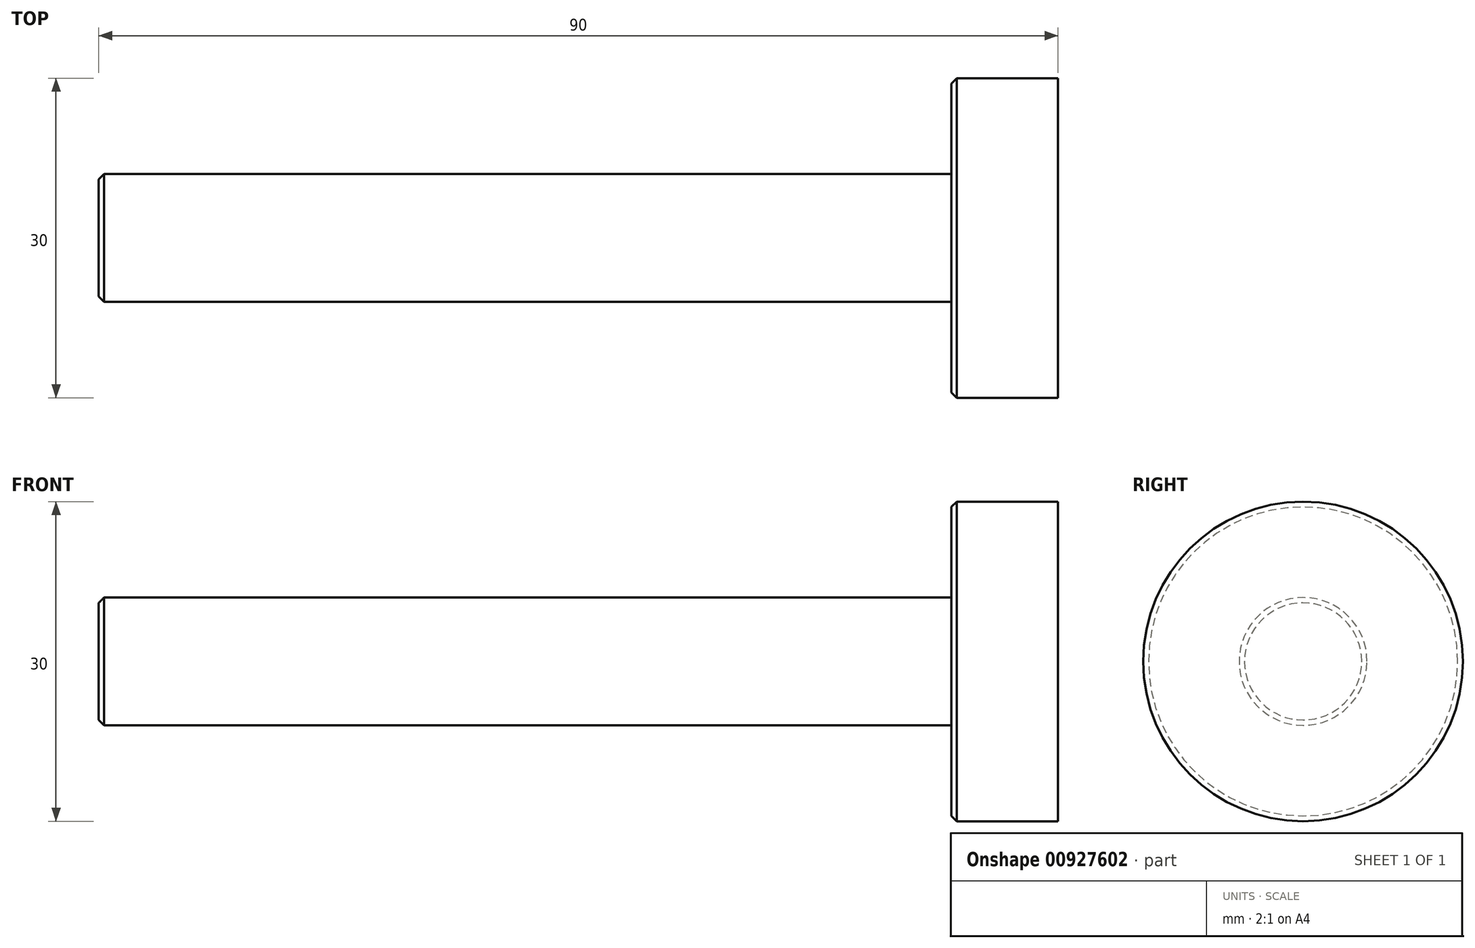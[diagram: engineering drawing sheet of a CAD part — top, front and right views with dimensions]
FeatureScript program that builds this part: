
annotation { "Feature Type Name" : "Feature", "Feature Type Description" : "" }
export const myFeature = defineFeature(function(context is Context, id is Id, definition is map)
    precondition{}
    {
        {
            var Q0;
            Q0=qCreatedBy(makeId("Right.planeOp"),FACE);
            var sketch = newSketch(context, id + "F0", { "sketchPlane" : qUnion([Q0])});
            skCircle(sketch, "E0", {"center": v(0, 0) * mm, "radius": 15 * mm});
            skSolve(sketch);
        }
        {
            var Q0;
            Q0 = qSketchRegion(id + "F0", true);
            extrude(context, id + "F1", {"entities" : qUnion([Q0]), "oppositeDirection" : true, "depth" : 10 * mm, "offsetDistance" : 25 * mm});
        }
        {
            var Q0;
            Q0=makeQuery(id+"F1.opExtrude","CAP_FACE",FACE,{"disambiguationData":[OSD([sQuery(id+"F0.wireOp",EDGE,"E0")])],"isStart":false});
            var sketch = newSketch(context, id + "F2", { "sketchPlane" : qUnion([Q0])});
            skCircle(sketch, "E1", {"center": v(0, 0) * mm, "radius": 6 * mm});
            skSolve(sketch);
        }
        {
            var Q0;
            Q0 = qSketchRegion(id + "F2", true);
            extrude(context, id + "F3", {"entities" : qUnion([Q0]), "operationType" : NewBodyOperationType.ADD, "depth" : 80 * mm, "offsetDistance" : 25 * mm});
        }
        {
            var Q0;
            Q0=makeQuery(id+"F3.opExtrude","CAP_EDGE",EDGE,{"disambiguationData":[OSD([sQuery(id+"F2.wireOp",EDGE,"E1")])],"isStart":false});
            var Q1;
            Q1=makeQuery(id+"F1.opExtrude","CAP_EDGE",EDGE,{"disambiguationData":[OSD([sQuery(id+"F0.wireOp",EDGE,"E0")])],"isStart":false});
            chamfer(context, id + "F4", {"entities" : qUnion([Q0, Q1]), "width" : 0.5 * mm, "tangentPropagation" : true});
        }
    });
